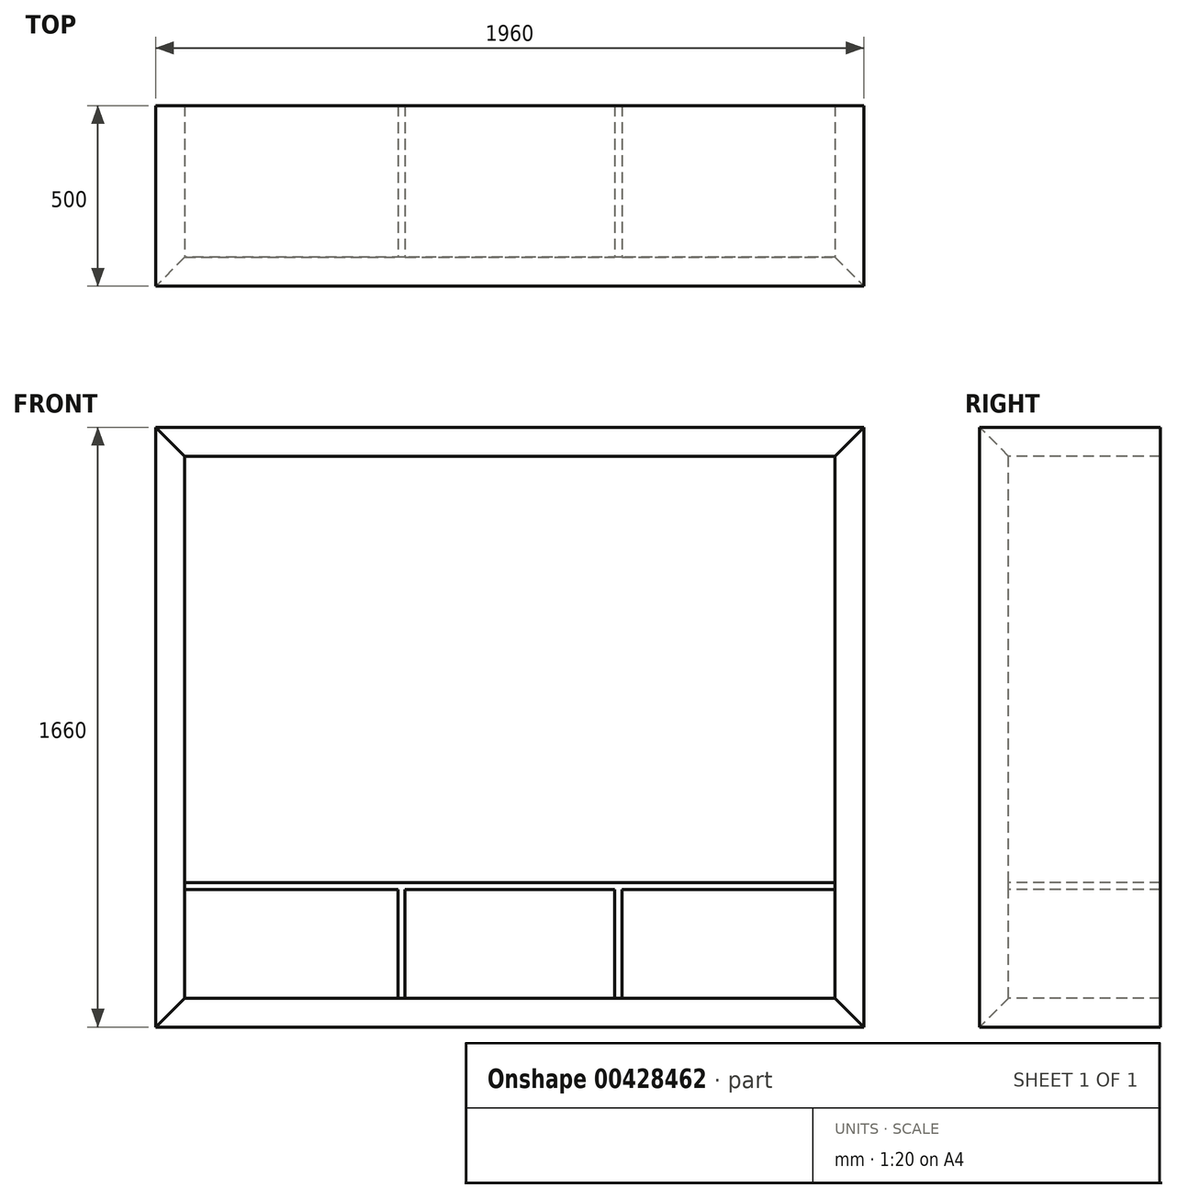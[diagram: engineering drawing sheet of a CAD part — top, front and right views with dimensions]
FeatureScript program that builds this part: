
annotation { "Feature Type Name" : "Feature", "Feature Type Description" : "" }
export const myFeature = defineFeature(function(context is Context, id is Id, definition is map)
    precondition{}
    {
        {
            var Q0;
            Q0=qCreatedBy(makeId("Front.planeOp"),FACE);
            var sketch = newSketch(context, id + "F0", { "sketchPlane" : qUnion([Q0])});
            skLineSegment(sketch, "E0.bottom", {"start": v(980, -830) * mm, "end": v(-980, -830) * mm});
            skLineSegment(sketch, "E0.top", {"start": v(980, 830) * mm, "end": v(-980, 830) * mm});
            skLineSegment(sketch, "E0.left", {"start": v(980, -830) * mm, "end": v(980, 830) * mm});
            skLineSegment(sketch, "E0.right", {"start": v(-980, -830) * mm, "end": v(-980, 830) * mm});
            skPoint(sketch, "E0.middle", {"position": v(0, 0) * mm});
            skLineSegment(sketch, "E1.0", {"start": v(-900, -750) * mm, "end": v(-900, 750) * mm});
            skLineSegment(sketch, "E2.0", {"start": v(900, -750) * mm, "end": v(-900, -750) * mm});
            skLineSegment(sketch, "E3.0", {"start": v(900, -750) * mm, "end": v(900, 750) * mm});
            skLineSegment(sketch, "E4.0", {"start": v(900, 750) * mm, "end": v(-900, 750) * mm});
            skLineSegment(sketch, "E5.0", {"start": v(900, -450) * mm, "end": v(-900, -450) * mm});
            skLineSegment(sketch, "E6.bottom", {"start": v(605, -189.4) * mm, "end": v(-605, -189.4) * mm});
            skLineSegment(sketch, "E6.top", {"start": v(605, 580.6) * mm, "end": v(-605, 580.6) * mm});
            skLineSegment(sketch, "E6.left", {"start": v(605, -189.4) * mm, "end": v(605, 580.6) * mm});
            skLineSegment(sketch, "E6.right", {"start": v(-605, -189.4) * mm, "end": v(-605, 580.6) * mm});
            skPoint(sketch, "E6.middle", {"position": v(0, 195.6) * mm});
            skLineSegment(sketch, "E7", {"start": v(-900, 750) * mm, "end": v(-980, 830) * mm});
            skLineSegment(sketch, "E8", {"start": v(-900, -750) * mm, "end": v(-980, -830) * mm});
            skLineSegment(sketch, "E9", {"start": v(900, -750) * mm, "end": v(980, -830) * mm});
            skLineSegment(sketch, "E10", {"start": v(980, 830) * mm, "end": v(900, 750) * mm});
            skLineSegment(sketch, "E11.0", {"start": v(900, -430) * mm, "end": v(-900, -430) * mm});
            skLineSegment(sketch, "E12.0", {"start": v(-290, -750) * mm, "end": v(-290, -450) * mm});
            skLineSegment(sketch, "E13.0", {"start": v(-310, -750) * mm, "end": v(-310, -450) * mm});
            skLineSegment(sketch, "E14.0", {"start": v(310, -750) * mm, "end": v(310, -450) * mm});
            skLineSegment(sketch, "E15.0", {"start": v(290, -750) * mm, "end": v(290, -450) * mm});
            skLineSegment(sketch, "E16.0", {"start": v(-300, -750) * mm, "end": v(-300, -450) * mm, "construction": true});
            skSolve(sketch);
        }
        {
            var Q0;
            Q0 = qSketchRegion(id + "F0", true);
            extrude(context, id + "F1", {"entities" : qUnion([Q0]), "oppositeDirection" : true, "depth" : 500 * mm});
        }
        {
            var Q0;
            Q0=makeQuery(id+"F1.opExtrude","CAP_EDGE",EDGE,{"disambiguationData":[OSD([sQuery(id+"F0.wireOp",EDGE,"E1.0")])],"isStart":true});
            var Q1;
            Q1=makeQuery(id+"F1.opExtrude","CAP_EDGE",EDGE,{"disambiguationData":[OSD([sQuery(id+"F0.wireOp",EDGE,"E4.0")])],"isStart":true});
            var Q2;
            Q2=makeQuery(id+"F1.opExtrude","CAP_EDGE",EDGE,{"disambiguationData":[OSD([sQuery(id+"F0.wireOp",EDGE,"E3.0")])],"isStart":true});
            var Q3;
            Q3=makeQuery(id+"F1.opExtrude","CAP_EDGE",EDGE,{"disambiguationData":[OSD([sQuery(id+"F0.wireOp",EDGE,"E2.0")])],"isStart":true});
            chamfer(context, id + "F2", {"entities" : qUnion([Q0, Q1, Q2, Q3]), "width" : 80 * mm, "tangentPropagation" : true});
        }
        {
            var Q0;
            {var subQ7=sQuery(id+"F0.wireOp",EDGE,"E11.0");Q0=makeQuery(id+"F0.imprint","IMPRINT",FACE,{"disambiguationData":[TD([[makeQuery(id+"F0.imprint","IMPRINT",EDGE,{"derivedFrom":subQ7}),1.0]])]});}
            var Q1;
            {var subQ0=sQuery(id+"F0.wireOp",EDGE,"E12.0");Q1=makeQuery(id+"F0.imprint","IMPRINT",FACE,{"disambiguationData":[TD([[makeQuery(id+"F0.imprint","IMPRINT",EDGE,{"derivedFrom":subQ0}),1.0]])]});}
            var Q2;
            {var subQ0=sQuery(id+"F0.wireOp",EDGE,"E14.0");Q2=makeQuery(id+"F0.imprint","IMPRINT",FACE,{"disambiguationData":[TD([[makeQuery(id+"F0.imprint","IMPRINT",EDGE,{"derivedFrom":subQ0}),1.0]])]});}
            extrude(context, id + "F3", {"entities" : qUnion([Q0, Q1, Q2]), "operationType" : NewBodyOperationType.ADD, "oppositeDirection" : true, "depth" : 500 * mm, "hasSecondDirection" : true, "secondDirectionOppositeDirection" : false, "secondDirectionDepth" : -80 * mm});
        }
    });
